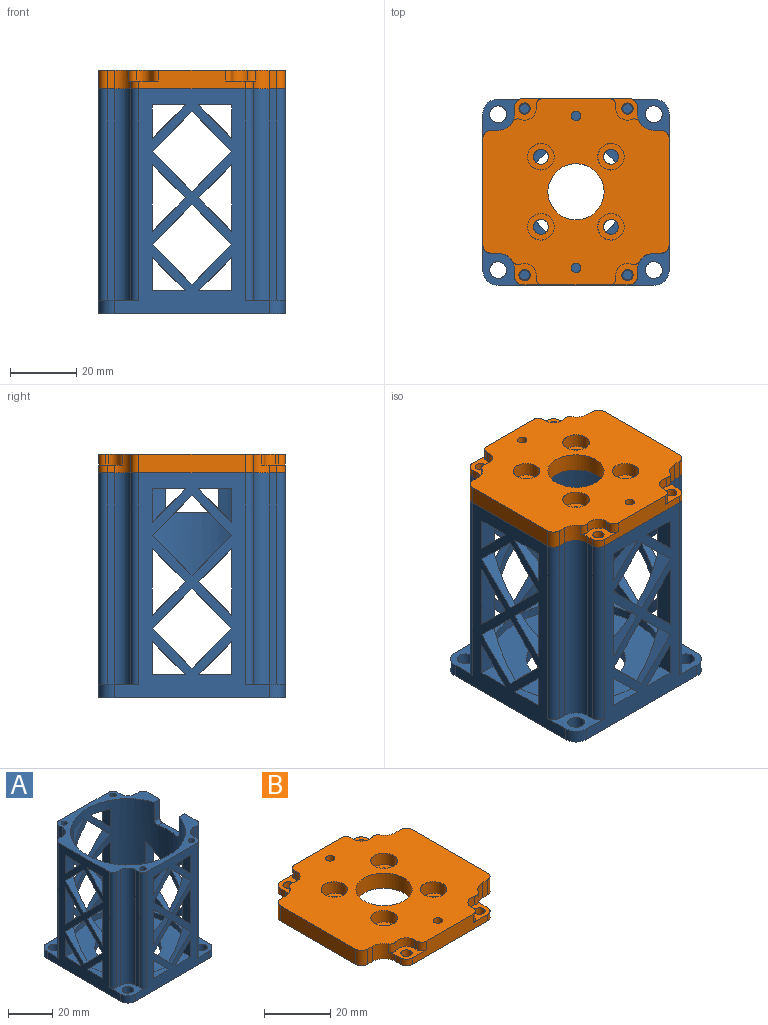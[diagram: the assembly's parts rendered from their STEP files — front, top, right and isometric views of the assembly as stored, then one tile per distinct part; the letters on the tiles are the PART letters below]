
ASSEMBLY  parts=2 mates=1
PART A: 148 faces, bbox 56.8x56.8x68.4 mm
  f0: cylinder r=26mm len=64mm, axis (0,0,-1), area 6546.1mm2, adj f5,f6,f12,f33,f34,f35,f37,f54
  f1: plane 68x47.2mm, normal (0,1,0), area 1257.2mm2, adj f12,f13,f32,f36,f38,f41,f44,f45
  f2: plane 68x47.2mm, normal (-1,0,0), area 1257.2mm2, adj f12,f17,f18,f36,f40,f41,f43,f44
  f3: plane 68x47.2mm, normal (0,-1,0), area 1257.2mm2, adj f12,f22,f23,f36,f39,f40,f42,f43
  f4: plane 68x47.2mm, normal (1,0,0), area 1460mm2, adj f5,f6,f12,f27,f28,f33,f34,f35
  f5: plane 10x3.46mm, normal (0,-1,0), area 34.6mm2, adj f0,f4,f6,f12
  f6: cylinder r=2mm len=3.46mm, axis (-1,0,0), area 10.1mm2, adj f0,f4,f5,f34
  f7: cylinder r=2.55mm len=5.1mm, axis (0,0,-1), area 64.1mm2, adj f36,f39
  f8: cylinder r=2.55mm len=5.1mm, axis (0,0,-1), area 64.1mm2, adj f36,f40
  f9: cylinder r=2.55mm len=5.1mm, axis (0,0,-1), area 64.1mm2, adj f36,f38
  f10: cylinder r=2.55mm len=5.1mm, axis (0,0,-1), area 64.1mm2, adj f36,f41
  f11: cylinder r=15mm len=30mm, axis (0,0,-1), area 377mm2, adj f36,f37
  f12: plane 56.4x56.4mm, normal (0,0,1), area 629mm2, adj f0,f1,f2,f3,f4,f5,f13,f14
  f13: cylinder r=2.5mm len=64mm, axis (0,0,-1), area 251.3mm2, adj f1,f12,f14,f41
  f14: plane 64x2.13mm, normal (-1,0,0), area 136.1mm2, adj f12,f13,f15,f41
  f15: cylinder r=5mm len=64mm, axis (0,0,-1), area 502.7mm2, adj f12,f14,f16,f41
  f16: plane 64x2.13mm, normal (0,1,0), area 136.1mm2, adj f12,f15,f17,f41
  f17: cylinder r=2.5mm len=64mm, axis (0,0,-1), area 251.3mm2, adj f2,f12,f16,f41
  f18: cylinder r=2.5mm len=64mm, axis (0,0,-1), area 251.3mm2, adj f2,f12,f19,f40
  f19: plane 64x2.13mm, normal (0,-1,0), area 136.1mm2, adj f12,f18,f20,f40
  f20: cylinder r=5mm len=64mm, axis (0,0,-1), area 502.7mm2, adj f12,f19,f21,f40
  f21: plane 64x2.13mm, normal (-1,0,0), area 136.1mm2, adj f12,f20,f22,f40
  f22: cylinder r=2.5mm len=64mm, axis (0,0,-1), area 251.3mm2, adj f3,f12,f21,f40
  f23: cylinder r=2.5mm len=64mm, axis (0,0,-1), area 251.3mm2, adj f3,f12,f24,f39
  f24: plane 64x2.13mm, normal (1,0,0), area 136.1mm2, adj f12,f23,f25,f39
  f25: cylinder r=5mm len=64mm, axis (0,0,-1), area 502.7mm2, adj f12,f24,f26,f39
  f26: plane 64x2.13mm, normal (0,-1,0), area 136.1mm2, adj f12,f25,f27,f39
  f27: cylinder r=2.5mm len=64mm, axis (0,0,-1), area 251.3mm2, adj f4,f12,f26,f39
  f28: cylinder r=2.5mm len=64mm, axis (0,0,-1), area 251.3mm2, adj f4,f12,f29,f38
  f29: plane 64x2.13mm, normal (0,1,0), area 136.1mm2, adj f12,f28,f30,f38
  f30: cylinder r=5mm len=64mm, axis (0,0,-1), area 502.7mm2, adj f12,f29,f31,f38
  f31: plane 64x2.13mm, normal (1,0,0), area 136.1mm2, adj f12,f30,f32,f38
  f32: cylinder r=2.5mm len=64mm, axis (0,0,-1), area 251.3mm2, adj f1,f12,f31,f38
  f33: plane 10x3.46mm, normal (0,1,0), area 34.6mm2, adj f0,f4,f12,f35
  f34: plane 12x2.9mm, normal (0,0,1), area 29.2mm2, adj f0,f4,f6,f35
  f35: cylinder r=2mm len=3.46mm, axis (-1,0,0), area 10.1mm2, adj f0,f4,f33,f34
  f36: plane 56.4x56.4mm, normal (0,0,-1), area 2374.2mm2, adj f1,f2,f3,f4,f7,f8,f9,f10
  f37: plane 52x52mm, normal (0,0,1), area 1416.9mm2, adj f0,f11
  f38: plane 12.13x12.13mm, normal (0,0,1), area 65mm2, adj f1,f4,f9,f28,f29,f30,f31,f32
  f39: plane 12.13x12.13mm, normal (0,0,1), area 65mm2, adj f3,f4,f7,f23,f24,f25,f26,f27
  f40: plane 12.13x12.13mm, normal (0,0,1), area 65mm2, adj f2,f3,f8,f18,f19,f20,f21,f22
  f41: plane 12.13x12.13mm, normal (0,0,1), area 65mm2, adj f1,f2,f10,f13,f14,f15,f16,f17
  f42: cylinder r=4.6mm len=4.6mm, axis (0,0,-1), area 28.9mm2, adj f3,f4,f36,f39
  f43: cylinder r=4.6mm len=4.6mm, axis (0,0,-1), area 28.9mm2, adj f2,f3,f36,f40
  f44: cylinder r=4.6mm len=4.6mm, axis (0,0,-1), area 28.9mm2, adj f1,f2,f36,f41
  f45: cylinder r=4.6mm len=4.6mm, axis (0,0,-1), area 28.9mm2, adj f1,f4,f36,f38
  f46: cylinder r=1.45mm len=14mm, axis (0,0,1), area 127.5mm2, adj f12,f50
  f47: cylinder r=1.45mm len=14mm, axis (0,0,1), area 127.5mm2, adj f12,f51
  f48: cylinder r=1.45mm len=14mm, axis (0,0,1), area 127.5mm2, adj f12,f52
  f49: cylinder r=1.45mm len=14mm, axis (0,0,1), area 127.5mm2, adj f12,f53
  f50: plane 2.9x2.9mm, normal (0,0,1), area 6.6mm2, adj f46
  f51: plane 2.9x2.9mm, normal (0,0,1), area 6.6mm2, adj f47
  f52: plane 2.9x2.9mm, normal (0,0,1), area 6.6mm2, adj f48
  f53: plane 2.9x2.9mm, normal (0,0,1), area 6.6mm2, adj f49
  f54: plane 12.44x12.44mm, normal (0,-0.71,-0.71), area 54.1mm2, adj f0,f4,f55,f57
  f55: plane 12.17x12.17mm, normal (0,0.71,-0.71), area 54.1mm2, adj f0,f4,f54,f56
  f56: plane 12.17x12.17mm, normal (0,0.71,0.71), area 54.1mm2, adj f0,f4,f55,f57
  f57: plane 12.44x12.44mm, normal (0,-0.71,0.71), area 54.1mm2, adj f0,f4,f54,f56
  f58: plane 10.15x10.15mm, normal (0,-0.71,-0.71), area 47.8mm2, adj f0,f4,f59,f60
  f59: plane 10.07x5.17mm, normal (0,0,1), area 33.8mm2, adj f0,f4,f58,f60
  f60: plane 10.07x5.17mm, normal (0,1,0), area 52.1mm2, adj f0,f4,f58,f59
  f61: plane 10.37x10.37mm, normal (0,0.71,-0.71), area 47.8mm2, adj f0,f4,f62,f63
  f62: plane 10.07x5.17mm, normal (0,0,1), area 33.8mm2, adj f0,f4,f61,f63
  f63: plane 10.07x5.17mm, normal (0,-1,0), area 52.1mm2, adj f0,f4,f61,f62
  f64: plane 10.15x10.15mm, normal (0,-0.71,-0.71), area 47.8mm2, adj f0,f4,f65,f66
  f65: plane 10.15x10.15mm, normal (0,-0.71,0.71), area 47.8mm2, adj f0,f4,f64,f66
  f66: plane 20.15x5.17mm, normal (0,1,0), area 104.2mm2, adj f0,f4,f64,f65
  f67: plane 10.37x10.37mm, normal (0,0.71,0.71), area 47.8mm2, adj f0,f4,f68,f69
  f68: plane 20.15x5.17mm, normal (0,-1,0), area 104.2mm2, adj f0,f4,f67,f69
  f69: plane 10.37x10.37mm, normal (0,0.71,-0.71), area 47.8mm2, adj f0,f4,f67,f68
  f70: plane 12.44x12.44mm, normal (-0.71,0,-0.71), area 54.1mm2, adj f0,f3,f72,f73
  f71: plane 12.44x12.44mm, normal (0.71,0,0.71), area 54.1mm2, adj f0,f3,f72,f73
  f72: plane 12.44x12.44mm, normal (-0.71,0,0.71), area 54.1mm2, adj f0,f3,f70,f71
  f73: plane 12.44x12.44mm, normal (0.71,0,-0.71), area 54.1mm2, adj f0,f3,f70,f71
  f74: plane 10.07x5.17mm, normal (-1,0,0), area 52.1mm2, adj f0,f3,f75,f76
  f75: plane 10.37x10.37mm, normal (0.71,0,0.71), area 47.8mm2, adj f0,f3,f74,f76
  f76: plane 10.07x5.17mm, normal (0,0,-1), area 33.8mm2, adj f0,f3,f74,f75
  f77: plane 12.44x12.44mm, normal (0.71,0,0.71), area 54.1mm2, adj f0,f3,f78,f79
  f78: plane 12.44x12.44mm, normal (-0.71,0,0.71), area 54.1mm2, adj f0,f3,f77,f80
  f79: plane 12.44x12.44mm, normal (0.71,0,-0.71), area 54.1mm2, adj f0,f3,f77,f80
  f80: plane 12.44x12.44mm, normal (-0.71,0,-0.71), area 54.1mm2, adj f0,f3,f78,f79
  f81: plane 10.07x5.17mm, normal (0,0,-1), area 33.8mm2, adj f0,f3,f82,f83
  f82: plane 10.07x5.17mm, normal (1,0,0), area 52.1mm2, adj f0,f3,f81,f83
  f83: plane 10.37x10.37mm, normal (-0.71,0,0.71), area 47.8mm2, adj f0,f3,f81,f82
  f84: plane 10.37x10.37mm, normal (-0.71,0,-0.71), area 47.8mm2, adj f0,f3,f85,f86
  f85: plane 10.07x5.17mm, normal (0,0,1), area 33.8mm2, adj f0,f3,f84,f86
  f86: plane 10.07x5.17mm, normal (1,0,0), area 52.1mm2, adj f0,f3,f84,f85
  f87: plane 10.37x10.37mm, normal (0.71,0,-0.71), area 47.8mm2, adj f0,f3,f88,f89
  f88: plane 10.07x5.17mm, normal (0,0,1), area 33.8mm2, adj f0,f3,f87,f89
  f89: plane 10.07x5.17mm, normal (-1,0,0), area 52.1mm2, adj f0,f3,f87,f88
  f90: plane 10.37x10.37mm, normal (-0.71,0,-0.71), area 47.8mm2, adj f0,f3,f91,f92
  f91: plane 10.37x10.37mm, normal (-0.71,0,0.71), area 47.8mm2, adj f0,f3,f90,f92
  f92: plane 20.15x5.17mm, normal (1,0,0), area 104.2mm2, adj f0,f3,f90,f91
  f93: plane 10.37x10.37mm, normal (0.71,0,-0.71), area 47.8mm2, adj f0,f3,f94,f95
  f94: plane 10.37x10.37mm, normal (0.71,0,0.71), area 47.8mm2, adj f0,f3,f93,f95
  f95: plane 20.15x5.17mm, normal (-1,0,0), area 104.2mm2, adj f0,f3,f93,f94
  f96: plane 12.44x12.44mm, normal (0,-0.71,-0.71), area 54.1mm2, adj f0,f2,f97,f98
  f97: plane 12.44x12.44mm, normal (0,0.71,-0.71), area 54.1mm2, adj f0,f2,f96,f99
  f98: plane 12.44x12.44mm, normal (0,-0.71,0.71), area 54.1mm2, adj f0,f2,f96,f99
  f99: plane 12.44x12.44mm, normal (0,0.71,0.71), area 54.1mm2, adj f0,f2,f97,f98
  f100: plane 10.07x5.17mm, normal (0,0,-1), area 33.8mm2, adj f0,f2,f101,f102
  f101: plane 10.07x5.17mm, normal (0,1,0), area 52.1mm2, adj f0,f2,f100,f102
  f102: plane 10.37x10.37mm, normal (0,-0.71,0.71), area 47.8mm2, adj f0,f2,f100,f101
  f103: plane 12.44x12.44mm, normal (0,-0.71,0.71), area 54.1mm2, adj f0,f2,f104,f105
  f104: plane 12.44x12.44mm, normal (0,0.71,0.71), area 54.1mm2, adj f0,f2,f103,f106
  f105: plane 12.44x12.44mm, normal (0,-0.71,-0.71), area 54.1mm2, adj f0,f2,f103,f106
  f106: plane 12.44x12.44mm, normal (0,0.71,-0.71), area 54.1mm2, adj f0,f2,f104,f105
  f107: plane 10.37x10.37mm, normal (0,0.71,0.71), area 47.8mm2, adj f0,f2,f108,f109
  f108: plane 10.07x5.17mm, normal (0,0,-1), area 33.8mm2, adj f0,f2,f107,f109
  f109: plane 10.07x5.17mm, normal (0,-1,0), area 52.1mm2, adj f0,f2,f107,f108
  f110: plane 10.37x10.37mm, normal (0,0.71,-0.71), area 47.8mm2, adj f0,f2,f111,f112
  f111: plane 10.07x5.17mm, normal (0,0,1), area 33.8mm2, adj f0,f2,f110,f112
  f112: plane 10.07x5.17mm, normal (0,-1,0), area 52.1mm2, adj f0,f2,f110,f111
  f113: plane 10.37x10.37mm, normal (0,-0.71,-0.71), area 47.8mm2, adj f0,f2,f114,f115
  f114: plane 10.07x5.17mm, normal (0,0,1), area 33.8mm2, adj f0,f2,f113,f115
  f115: plane 10.07x5.17mm, normal (0,1,0), area 52.1mm2, adj f0,f2,f113,f114
  f116: plane 10.37x10.37mm, normal (0,0.71,-0.71), area 47.8mm2, adj f0,f2,f117,f118
  f117: plane 10.37x10.37mm, normal (0,0.71,0.71), area 47.8mm2, adj f0,f2,f116,f118
  f118: plane 20.15x5.17mm, normal (0,-1,0), area 104.2mm2, adj f0,f2,f116,f117
  f119: plane 10.37x10.37mm, normal (0,-0.71,0.71), area 47.8mm2, adj f0,f2,f120,f121
  f120: plane 10.37x10.37mm, normal (0,-0.71,-0.71), area 47.8mm2, adj f0,f2,f119,f121
  f121: plane 20.15x5.17mm, normal (0,1,0), area 104.2mm2, adj f0,f2,f119,f120
  f122: plane 12.44x12.44mm, normal (-0.71,0,-0.71), area 54.1mm2, adj f0,f1,f123,f124
  f123: plane 12.44x12.44mm, normal (0.71,0,-0.71), area 54.1mm2, adj f0,f1,f122,f125
  f124: plane 12.44x12.44mm, normal (-0.71,0,0.71), area 54.1mm2, adj f0,f1,f122,f125
  f125: plane 12.44x12.44mm, normal (0.71,0,0.71), area 54.1mm2, adj f0,f1,f123,f124
  f126: plane 10.07x5.17mm, normal (0,0,-1), area 33.8mm2, adj f0,f1,f127,f128
  f127: plane 10.07x5.17mm, normal (1,0,0), area 52.1mm2, adj f0,f1,f126,f128
  f128: plane 10.37x10.37mm, normal (-0.71,0,0.71), area 47.8mm2, adj f0,f1,f126,f127
  f129: plane 12.44x12.44mm, normal (-0.71,0,0.71), area 54.1mm2, adj f0,f1,f130,f131
  f130: plane 12.44x12.44mm, normal (0.71,0,0.71), area 54.1mm2, adj f0,f1,f129,f132
  f131: plane 12.44x12.44mm, normal (-0.71,0,-0.71), area 54.1mm2, adj f0,f1,f129,f132
  f132: plane 12.44x12.44mm, normal (0.71,0,-0.71), area 54.1mm2, adj f0,f1,f130,f131
  f133: plane 10.37x10.37mm, normal (0.71,0,0.71), area 47.8mm2, adj f0,f1,f134,f135
  f134: plane 10.07x5.17mm, normal (0,0,-1), area 33.8mm2, adj f0,f1,f133,f135
  f135: plane 10.07x5.17mm, normal (-1,0,0), area 52.1mm2, adj f0,f1,f133,f134
  f136: plane 10.37x10.37mm, normal (0.71,0,-0.71), area 47.8mm2, adj f0,f1,f137,f138
  f137: plane 10.07x5.17mm, normal (0,0,1), area 33.8mm2, adj f0,f1,f136,f138
  f138: plane 10.07x5.17mm, normal (-1,0,0), area 52.1mm2, adj f0,f1,f136,f137
  f139: plane 10.37x10.37mm, normal (-0.71,0,-0.71), area 47.8mm2, adj f0,f1,f140,f141
  f140: plane 10.07x5.17mm, normal (0,0,1), area 33.8mm2, adj f0,f1,f139,f141
  f141: plane 10.07x5.17mm, normal (1,0,0), area 52.1mm2, adj f0,f1,f139,f140
  f142: plane 10.37x10.37mm, normal (0.71,0,-0.71), area 47.8mm2, adj f0,f1,f143,f144
  f143: plane 10.37x10.37mm, normal (0.71,0,0.71), area 47.8mm2, adj f0,f1,f142,f144
  f144: plane 20.15x5.17mm, normal (-1,0,0), area 104.2mm2, adj f0,f1,f142,f143
  f145: plane 10.37x10.37mm, normal (-0.71,0,0.71), area 47.8mm2, adj f0,f1,f146,f147
  f146: plane 10.37x10.37mm, normal (-0.71,0,-0.71), area 47.8mm2, adj f0,f1,f145,f147
  f147: plane 20.15x5.17mm, normal (1,0,0), area 104.2mm2, adj f0,f1,f145,f146
PART B: 69 faces, bbox 56.4x56.4x5.6 mm
  f0: plane 3.2x1mm, normal (1,0,0), area 3.2mm2, adj f1,f32,f60,f65
  f1: cylinder r=3.5mm len=4.74mm, axis (0,0,1), area 21.6mm2, adj f0,f32,f60,f63
  f2: plane 3.2x1mm, normal (-1,0,0), area 3.2mm2, adj f3,f32,f59,f62
  f3: cylinder r=3.5mm len=4.74mm, axis (0,0,1), area 21.6mm2, adj f2,f32,f59,f67
  f4: plane 3.2x1mm, normal (1,0,0), area 3.2mm2, adj f5,f32,f58,f61
  f5: cylinder r=3.5mm len=4.74mm, axis (0,0,1), area 21.6mm2, adj f4,f32,f58,f68
  f6: plane 3.2x1mm, normal (-1,0,0), area 3.2mm2, adj f7,f32,f57,f66
  f7: cylinder r=3.5mm len=4.74mm, axis (0,0,1), area 21.6mm2, adj f6,f32,f57,f64
  f8: cylinder r=1.44mm len=5.6mm, axis (0,0,1), area 50.5mm2, adj f31,f32
  f9: cylinder r=1.44mm len=5.6mm, axis (0,0,1), area 50.5mm2, adj f31,f32
  f10: cylinder r=1.7mm len=3.4mm, axis (0,0,1), area 25.6mm2, adj f31,f59
  f11: cylinder r=1.7mm len=3.4mm, axis (0,0,1), area 25.6mm2, adj f31,f60
  f12: cylinder r=1.7mm len=3.4mm, axis (0,0,1), area 25.6mm2, adj f31,f58
  f13: cylinder r=1.7mm len=3.4mm, axis (0,0,1), area 25.6mm2, adj f31,f57
  f14: cone r=4.03mm half-angle=45deg, axis (0,0,1), area 0.9mm2, adj f15,f32
  f15: cylinder r=4mm len=8mm, axis (0,0,1), area 106.2mm2, adj f14,f36
  f16: cylinder r=2.25mm len=4.5mm, axis (0,0,1), area 19.1mm2, adj f31,f36
  f17: cone r=4.03mm half-angle=45deg, axis (0,0,1), area 0.9mm2, adj f18,f32
  f18: cylinder r=4mm len=8mm, axis (0,0,1), area 106.2mm2, adj f17,f35
  f19: cylinder r=2.25mm len=4.5mm, axis (0,0,1), area 19.1mm2, adj f31,f35
  f20: cone r=4.03mm half-angle=45deg, axis (0,0,1), area 0.9mm2, adj f21,f32
  f21: cylinder r=4mm len=8mm, axis (0,0,1), area 106.2mm2, adj f20,f34
  f22: cylinder r=2.25mm len=4.5mm, axis (0,0,1), area 19.1mm2, adj f31,f34
  f23: cone r=4.03mm half-angle=45deg, axis (0,0,1), area 0.9mm2, adj f24,f32
  f24: cylinder r=4mm len=8mm, axis (0,0,1), area 106.2mm2, adj f23,f33
  f25: cylinder r=2.25mm len=4.5mm, axis (0,0,1), area 19.1mm2, adj f31,f33
  f26: cylinder r=8.5mm len=17mm, axis (0,0,1), area 299.1mm2, adj f31,f32
  f27: plane 32.15x5.6mm, normal (0,-1,0), area 141.6mm2, adj f31,f32,f37,f44,f59,f60,f62,f65
  f28: plane 32.15x5.6mm, normal (0,1,0), area 141.6mm2, adj f31,f32,f47,f54,f57,f58,f61,f66
  f29: plane 32.15x5.6mm, normal (1,0,0), area 180mm2, adj f31,f32,f45,f51
  f30: plane 32.15x5.6mm, normal (-1,0,0), area 180mm2, adj f31,f32,f41,f53
  f31: plane 56.4x56.4mm, normal (0,0,-1), area 2481.1mm2, adj f8,f9,f10,f11,f12,f13,f16,f19
  f32: plane 56.4x56.4mm, normal (0,0,1), area 2222.2mm2, adj f0,f1,f2,f3,f4,f5,f6,f7
  f33: plane 8x8mm, normal (0,0,1), area 34.4mm2, adj f24,f25
  f34: plane 8x8mm, normal (0,0,1), area 34.4mm2, adj f21,f22
  f35: plane 8x8mm, normal (0,0,1), area 34.4mm2, adj f18,f19
  f36: plane 8x8mm, normal (0,0,1), area 34.4mm2, adj f15,f16
  f37: cylinder r=2.5mm len=2.5mm, axis (0,0,-1), area 9.4mm2, adj f27,f31,f38,f59
  f38: plane 2.4x2.13mm, normal (-1,0,0), area 5.1mm2, adj f31,f37,f39,f59
  f39: cylinder r=5mm len=5.6mm, axis (0,0,-1), area 35.6mm2, adj f31,f32,f38,f40,f59,f67
  f40: plane 5.6x2.13mm, normal (0,-1,0), area 11.9mm2, adj f31,f32,f39,f41
  f41: cylinder r=2.5mm len=5.6mm, axis (0,0,-1), area 22mm2, adj f30,f31,f32,f40
  f42: cylinder r=5mm len=5.6mm, axis (0,0,-1), area 35.6mm2, adj f31,f32,f43,f46,f60,f63
  f43: plane 2.4x2.13mm, normal (1,0,0), area 5.1mm2, adj f31,f42,f44,f60
  f44: cylinder r=2.5mm len=2.5mm, axis (0,0,-1), area 9.4mm2, adj f27,f31,f43,f60
  f45: cylinder r=2.5mm len=5.6mm, axis (0,0,-1), area 22mm2, adj f29,f31,f32,f46
  f46: plane 5.6x2.13mm, normal (0,-1,0), area 11.9mm2, adj f31,f32,f42,f45
  f47: cylinder r=2.5mm len=2.5mm, axis (0,0,-1), area 9.4mm2, adj f28,f31,f48,f58
  f48: plane 2.4x2.13mm, normal (1,0,0), area 5.1mm2, adj f31,f47,f49,f58
  f49: cylinder r=5mm len=5.6mm, axis (0,0,-1), area 35.6mm2, adj f31,f32,f48,f50,f58,f68
  f50: plane 5.6x2.13mm, normal (0,1,0), area 11.9mm2, adj f31,f32,f49,f51
  f51: cylinder r=2.5mm len=5.6mm, axis (0,0,-1), area 22mm2, adj f29,f31,f32,f50
  f52: plane 5.6x2.13mm, normal (0,1,0), area 11.9mm2, adj f31,f32,f53,f56
  f53: cylinder r=2.5mm len=5.6mm, axis (0,0,-1), area 22mm2, adj f30,f31,f32,f52
  f54: cylinder r=2.5mm len=2.5mm, axis (0,0,-1), area 9.4mm2, adj f28,f31,f55,f57
  f55: plane 2.4x2.13mm, normal (-1,0,0), area 5.1mm2, adj f31,f54,f56,f57
  f56: cylinder r=5mm len=5.6mm, axis (0,0,-1), area 35.6mm2, adj f31,f32,f52,f55,f57,f64
  f57: plane 9.18x7.14mm, normal (0,0,1), area 29.7mm2, adj f6,f7,f13,f28,f54,f55,f56,f64
  f58: plane 9.18x7.14mm, normal (0,0,1), area 29.7mm2, adj f4,f5,f12,f28,f47,f48,f49,f61
  f59: plane 9.18x7.14mm, normal (0,0,1), area 29.7mm2, adj f2,f3,f10,f27,f37,f38,f39,f62
  f60: plane 9.18x7.14mm, normal (0,0,1), area 29.7mm2, adj f0,f1,f11,f27,f42,f43,f44,f63
  f61: cylinder r=2mm len=3.2mm, axis (0,0,-1), area 10.1mm2, adj f4,f28,f32,f58
  f62: cylinder r=2mm len=3.2mm, axis (0,0,-1), area 10.1mm2, adj f2,f27,f32,f59
  f63: cylinder r=2mm len=3.2mm, axis (0,0,-1), area 9mm2, adj f1,f32,f42,f60
  f64: cylinder r=2mm len=3.2mm, axis (0,0,-1), area 9mm2, adj f7,f32,f56,f57
  f65: cylinder r=2mm len=3.2mm, axis (0,0,1), area 10.1mm2, adj f0,f27,f32,f60
  f66: cylinder r=2mm len=3.2mm, axis (0,0,1), area 10.1mm2, adj f6,f28,f32,f57
  f67: cylinder r=2mm len=3.2mm, axis (0,0,1), area 9mm2, adj f3,f32,f39,f59
  f68: cylinder r=2mm len=3.2mm, axis (0,0,1), area 9mm2, adj f5,f32,f49,f58
PLACE A t=(0,0,-33)mm
PLACE B at identity fixed
MATE fastened A.f0 <-> B.f26  axis (0,0,-1) through (0,0,0)mm
